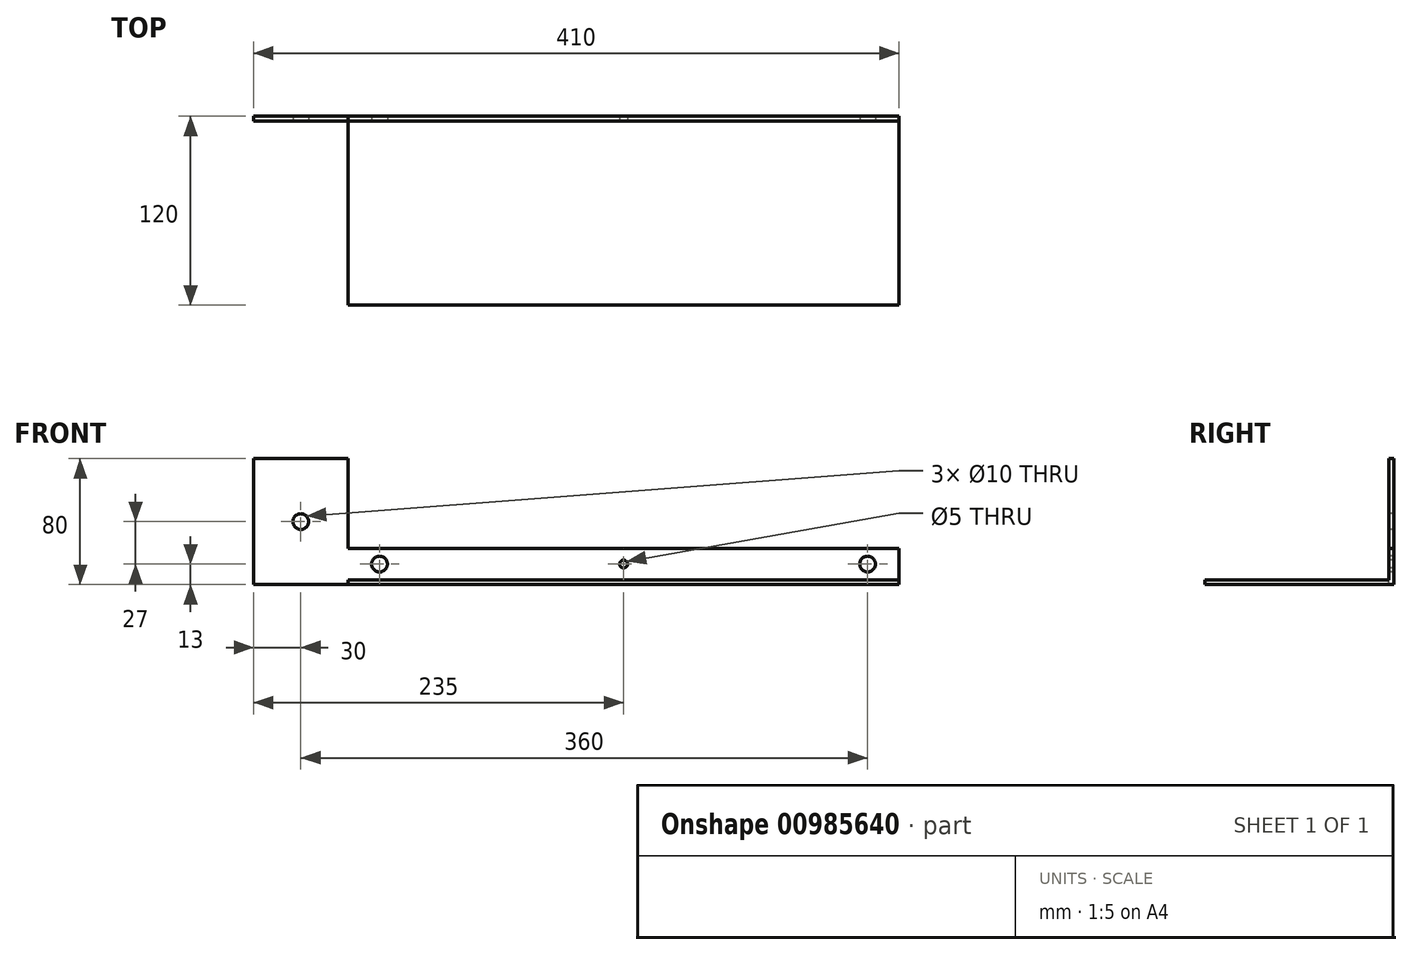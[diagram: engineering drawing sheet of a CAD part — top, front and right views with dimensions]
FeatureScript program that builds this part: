
annotation { "Feature Type Name" : "Feature", "Feature Type Description" : "" }
export const myFeature = defineFeature(function(context is Context, id is Id, definition is map)
    precondition{}
    {
        {
            var Q0;
            Q0=qCreatedBy(makeId("Top.planeOp"),FACE);
            var sketch = newSketch(context, id + "F0", { "sketchPlane" : qUnion([Q0])});
            skLineSegment(sketch, "E0.bottom", {"start": v(0, 0) * mm, "end": v(350, 0) * mm});
            skLineSegment(sketch, "E0.top", {"start": v(0, -120) * mm, "end": v(350, -120) * mm});
            skLineSegment(sketch, "E0.left", {"start": v(0, 0) * mm, "end": v(0, -120) * mm});
            skLineSegment(sketch, "E0.right", {"start": v(350, 0) * mm, "end": v(350, -120) * mm});
            skSolve(sketch);
        }
        {
            var Q0;
            Q0 = qSketchRegion(id + "F0", true);
            extrude(context, id + "F1", {"entities" : qUnion([Q0]), "depth" : 3 * mm, "offsetDistance" : 25 * mm});
        }
        {
            var Q0;
            Q0=makeQuery(id+"F1.opExtrude","SWEPT_FACE",FACE,{"disambiguationData":[OSD([sQuery(id+"F0.wireOp",EDGE,"E0.bottom")])]});
            var sketch = newSketch(context, id + "F2", { "sketchPlane" : qUnion([Q0])});
            skLineSegment(sketch, "E1.bottom", {"start": v(0, 0) * mm, "end": v(60, 0) * mm});
            skLineSegment(sketch, "E1.top", {"start": v(0, 80) * mm, "end": v(60, 80) * mm});
            skLineSegment(sketch, "E1.left", {"start": v(0, 0) * mm, "end": v(0, 80) * mm});
            skLineSegment(sketch, "E1.right", {"start": v(60, 0) * mm, "end": v(60, 80) * mm});
            skSolve(sketch);
        }
        {
            var Q0;
            Q0 = qSketchRegion(id + "F2", true);
            extrude(context, id + "F3", {"entities" : qUnion([Q0]), "operationType" : NewBodyOperationType.ADD, "oppositeDirection" : true, "depth" : 3 * mm, "offsetDistance" : 25 * mm});
        }
        {
            var Q0;
            Q0=makeQuery(id+"F3.opExtrude","CAP_FACE",FACE,{"disambiguationData":[OSD([sQuery(id+"F2.wireOp",EDGE,"E1.bottom"),sQuery(id+"F2.wireOp",EDGE,"E1.top"),sQuery(id+"F2.wireOp",EDGE,"E1.left"),sQuery(id+"F2.wireOp",EDGE,"E1.right")])],"isStart":false});
            var sketch = newSketch(context, id + "F4", { "sketchPlane" : qUnion([Q0])});
            skLineSegment(sketch, "E2", {"start": v(-60, 80) * mm, "end": v(0, 0) * mm, "construction": true});
            skLineSegment(sketch, "E3", {"start": v(0, 80) * mm, "end": v(-60, 0) * mm, "construction": true});
            skCircle(sketch, "E4", {"center": v(-30, 40) * mm, "radius": 5 * mm});
            skSolve(sketch);
        }
        {
            var Q0;
            Q0 = qSketchRegion(id + "F4", true);
            extrude(context, id + "F5", {"entities" : qUnion([Q0]), "operationType" : NewBodyOperationType.REMOVE, "oppositeDirection" : true, "depth" : 25 * mm, "offsetDistance" : 25 * mm});
        }
        {
            var Q0;
            Q0=makeQuery(id+"F1.opExtrude","CAP_FACE",FACE,{"disambiguationData":[OSD([sQuery(id+"F0.wireOp",EDGE,"E0.bottom"),sQuery(id+"F0.wireOp",EDGE,"E0.top"),sQuery(id+"F0.wireOp",EDGE,"E0.left"),sQuery(id+"F0.wireOp",EDGE,"E0.right")])],"isStart":false});
            var sketch = newSketch(context, id + "F6", { "sketchPlane" : qUnion([Q0])});
            skLineSegment(sketch, "E5.0", {"start": v(0, 0) * mm, "end": v(350, 0) * mm});
            skLineSegment(sketch, "E6.0", {"start": v(0, -3) * mm, "end": v(350, -3) * mm});
            skLineSegment(sketch, "E7.0", {"start": v(350, 0) * mm, "end": v(350, -3) * mm});
            skLineSegment(sketch, "E7.1", {"start": v(0, 0) * mm, "end": v(0, -3) * mm});
            skPoint(sketch, "E8.orphan", {"position": v(350, -120) * mm});
            skSolve(sketch);
        }
        {
            var Q0;
            Q0 = qSketchRegion(id + "F6", true);
            extrude(context, id + "F7", {"entities" : qUnion([Q0]), "operationType" : NewBodyOperationType.ADD, "depth" : 20 * mm, "offsetDistance" : 25 * mm});
        }
        {
            var Q0;
            Q0=makeQuery(id+"F7.boolean.opBoolean","MERGE",FACE,{"derivedFrom":[makeQuery(id+"F3.opExtrude","CAP_FACE",FACE,{"disambiguationData":[OSD([sQuery(id+"F2.wireOp",EDGE,"E1.bottom"),sQuery(id+"F2.wireOp",EDGE,"E1.top"),sQuery(id+"F2.wireOp",EDGE,"E1.left"),sQuery(id+"F2.wireOp",EDGE,"E1.right")])],"isStart":false}),makeQuery(id+"F7.opExtrude","SWEPT_FACE",FACE,{"disambiguationData":[OSD([sQuery(id+"F6.wireOp",EDGE,"E6.0")])]})]});
            var sketch = newSketch(context, id + "F8", { "sketchPlane" : qUnion([Q0])});
            skLineSegment(sketch, "E9", {"start": v(0, 23) * mm, "end": v(0, 3) * mm, "construction": true});
            skLineSegment(sketch, "E10", {"start": v(0, 13) * mm, "end": v(350, 13) * mm, "construction": true});
            skLineSegment(sketch, "E11.0", {"start": v(350, 23) * mm, "end": v(350, 3) * mm, "construction": true});
            skLineSegment(sketch, "E12.0", {"start": v(20, 23) * mm, "end": v(20, 3) * mm, "construction": true});
            skPoint(sketch, "E13.0.end.orphan", {"position": v(330, 3) * mm});
            skLineSegment(sketch, "E14", {"start": v(330, 3) * mm, "end": v(330, 23) * mm, "construction": true});
            skLineSegment(sketch, "E15.0", {"start": v(0, 3) * mm, "end": v(350, 3) * mm, "construction": true});
            skLineSegment(sketch, "E16.0", {"start": v(0, 23) * mm, "end": v(350, 23) * mm, "construction": true});
            skCircle(sketch, "E17", {"center": v(330, 13) * mm, "radius": 5 * mm});
            skCircle(sketch, "E18", {"center": v(20, 13) * mm, "radius": 5 * mm});
            skSolve(sketch);
        }
        {
            var Q0;
            Q0 = qSketchRegion(id + "F8", true);
            extrude(context, id + "F9", {"entities" : qUnion([Q0]), "operationType" : NewBodyOperationType.REMOVE, "oppositeDirection" : true, "depth" : 25 * mm, "offsetDistance" : 25 * mm});
        }
        {
            var Q0;
            Q0=makeQuery(id+"F1.opExtrude","CAP_FACE",FACE,{"disambiguationData":[OSD([sQuery(id+"F0.wireOp",EDGE,"E0.bottom"),sQuery(id+"F0.wireOp",EDGE,"E0.top"),sQuery(id+"F0.wireOp",EDGE,"E0.left"),sQuery(id+"F0.wireOp",EDGE,"E0.right")])],"isStart":false});
            var sketch = newSketch(context, id + "F10", { "sketchPlane" : qUnion([Q0])});
            skLineSegment(sketch, "E19.0", {"start": v(0, -120) * mm, "end": v(350, -120) * mm});
            skLineSegment(sketch, "E20.0", {"start": v(0, -117) * mm, "end": v(350, -117) * mm});
            skLineSegment(sketch, "E21.0", {"start": v(0, -117) * mm, "end": v(0, -120) * mm});
            skLineSegment(sketch, "E22.0", {"start": v(350, -117) * mm, "end": v(350, -120) * mm});
            skPoint(sketch, "E23.orphan", {"position": v(350, -3) * mm});
            skPoint(sketch, "E24.orphan", {"position": v(0, -3) * mm});
            skSolve(sketch);
        }
        {
            var Q0;
            Q0=makeQuery(id+"F8.imprint","IMPRINT",FACE,{"disambiguationData":[TD([[makeQuery(id+"F8.imprint","IMPRINT",EDGE,{"derivedFrom":sQuery(id+"F8.wireOp",EDGE,"E17")}),-1.0]])]});
            var sketch = newSketch(context, id + "F11", { "sketchPlane" : qUnion([Q0])});
            skLineSegment(sketch, "E25.0", {"start": v(0, 13) * mm, "end": v(350, 13) * mm, "construction": true});
            skCircle(sketch, "E26", {"center": v(175, 13) * mm, "radius": 2.5 * mm});
            skSolve(sketch);
        }
        {
            var Q0;
            Q0 = qSketchRegion(id + "F11", true);
            extrude(context, id + "F12", {"entities" : qUnion([Q0]), "operationType" : NewBodyOperationType.REMOVE, "oppositeDirection" : true, "depth" : 25 * mm, "offsetDistance" : 25 * mm});
        }
    });
